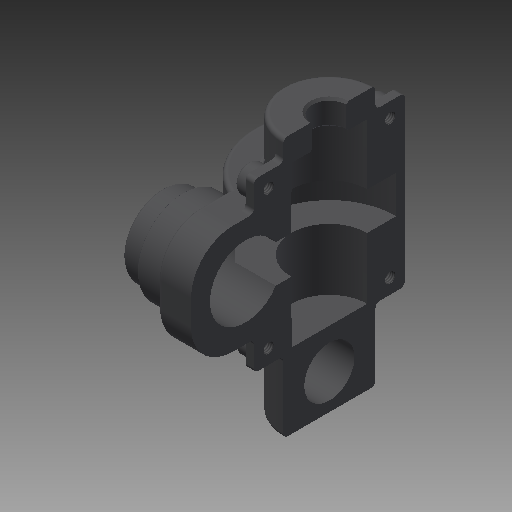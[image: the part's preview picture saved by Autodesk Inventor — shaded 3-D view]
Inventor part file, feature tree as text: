
AUTODESK INVENTOR PART (.ipt)
format: ipt  version: 2019 (Build 230136000, 136)  size: 435,712 bytes
history: native  units: mm
features: extrude x10, fillet x7, sketch x5, projected_geometry x2, plane x1, revolve x1, split x1, hole x1, chamfer x1
ambient origin geometry x8: Origin, YZ Plane, XZ Plane, XY Plane, X Axis, Y Axis, Z Axis, Center Point
bodies: Solid1 (feature_tree)
feature tree (29):
  extrude  "Extrusion1"  Depth=62.0mm TaperAngle=0.0deg
  plane  "Work Plane1"
  extrude  "Extrusion2"  Depth=36.0mm
  sketch  "Sketch3"  dims[d5=26.0mm d6=0.0mm d7=22.0mm]
  extrude  "Extrusion3"  Depth=22.0mm
  extrude  "Extrusion4"  Depth=15.0mm
  extrude  "Extrusion5"  Depth=1.0mm TaperAngle=0.0deg
  extrude  "Extrusion6"  Depth=1.0mm TaperAngle=0.0deg
  revolve  "Revolution1"  [1 undecoded]
  split  "Split1"
  extrude  "Extrusion7"  Depth=1.0mm
  extrude  "Extrusion8"  Depth=1.0mm TaperAngle=0.0deg
  fillet  "Fillet7"  Radius=34.0mm
  fillet  "Fillet8"  Radius=9.05mm
  fillet  "Fillet9"  Radius=9.0mm
  sketch  "Sketch5"  dims[d10=13.0mm d11=16.0mm d12=0.0mm d13=30.0mm d14=0.0mm d15=19.0mm d16=17.0mm d17=40.0mm d18=0.0mm d19=34.0mm d20=0.0mm d25=9.05mm d26=9.0mm d28=6.0mm d29=4.05mm d30=2.0mm d31=14.65mm d32=90.0deg d34=12.0mm d35=8.374731mm d36=56.0mm d37=0.0mm d40=10.0mm d41=56.0mm d42=0.0mm d47=10.0mm d48=1.0mm d49=0.5mm d51=7.0mm d52=7.0mm d53=3.5mm d54=3.5mm d56=2.0mm d57=0.0mm d67=26.0mm d78=6.5mm d79=6.5mm d80=6.5mm d81=6.5mm d82=5.0mm d83=0.0mm d84=2.459mm d85=6.0mm d86=6.3mm d87=2.0mm d88=90.0deg d89=4.0mm d90=20.594885mm d91=2.0mm d92=0.5mm d93=2.0mm d94=45.0deg d95=1.0mm d96=1.0mm d97=1.0mm d98=1.0mm d99=0.625269mm]
  extrude  "Extrusion9"  Depth=1.0mm
  extrude  "Extrusion11"  Depth=1.0mm
  hole  "Hole2"  [1 undecoded]
  chamfer  "Chamfer1"  Distance=14.65mm
  fillet  "Fillet13"  [1 undecoded]
  fillet  "Fillet14"  Radius=12.0mm
  fillet  "Fillet15"  Radius=8.374731mm
  fillet  "Fillet16"  Radius=56.0mm
  sketch  "Sketch1"  dims[d0=22.0mm d1=62.0mm d2=0.0mm]
  sketch  "Sketch2"  dims[d3=-24.0mm d4=36.0mm]
  sketch  "Sketch4"  dims[d8=20.0mm d9=15.0mm]
  projected_geometry  "Project Cut Edges1"
  projected_geometry  "Project Cut Edges2"
note: 3 required parameter values undecoded (feature->parameter linkage not recoverable at this tier; creation-order binding heuristic only, values carry confidence <= 0.55)